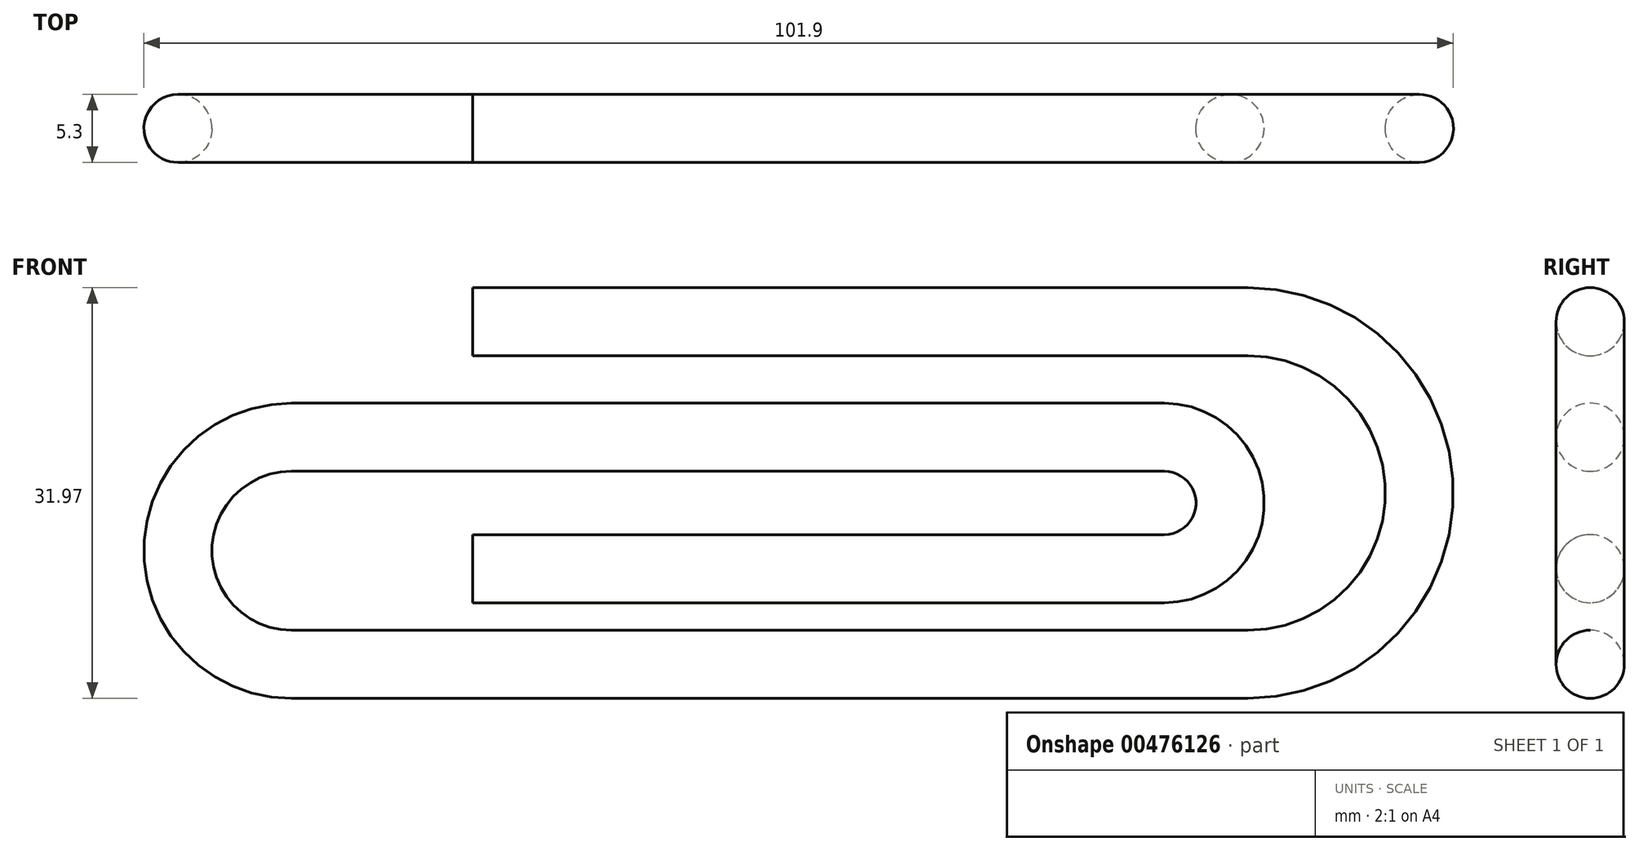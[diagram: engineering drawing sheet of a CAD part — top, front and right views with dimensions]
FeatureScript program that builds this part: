
annotation { "Feature Type Name" : "Feature", "Feature Type Description" : "" }
export const myFeature = defineFeature(function(context is Context, id is Id, definition is map)
    precondition{}
    {
        {
            var Q0;
            Q0=qCreatedBy(makeId("Front.planeOp"),FACE);
            cPlane(context, id + "F0", {"entities" : qUnion([Q0]), "cplaneType" : CPlaneType.OFFSET, "offset" : 25.4 * mm, "width" : 152.4 * mm, "height" : 152.4 * mm});
        }
        {
            var Q0;
            Q0=qCreatedBy(id+"F0.planeOp",FACE);
            var sketch = newSketch(context, id + "F1", { "sketchPlane" : qUnion([Q0])});
            skLineSegment(sketch, "E0", {"start": v(0, 0) * mm, "end": v(60.32, 0) * mm});
            skArc(sketch, "E1", {"start": v(60.32, -26.67) * mm, "mid": v(73.65, -13.34) * mm, "end": v(60.32, 0) * mm});
            skLineSegment(sketch, "E2", {"start": v(60.32, -26.67) * mm, "end": v(-14.11, -26.67) * mm});
            skArc(sketch, "E3", {"start": v(-14.11, -9) * mm, "mid": v(-22.95, -17.83) * mm, "end": v(-14.11, -26.67) * mm});
            skLineSegment(sketch, "E4", {"start": v(-14.11, -9) * mm, "end": v(53.8, -9) * mm});
            skArc(sketch, "E5", {"start": v(53.8, -19.23) * mm, "mid": v(58.92, -14.11) * mm, "end": v(53.8, -9) * mm});
            skLineSegment(sketch, "E6", {"start": v(53.8, -19.23) * mm, "end": v(0, -19.23) * mm});
            skSolve(sketch);
        }
        {
            var Q0;
            Q0=qCreatedBy(makeId("Right.planeOp"),FACE);
            var sketch = newSketch(context, id + "F2", { "sketchPlane" : qUnion([Q0])});
            skCircle(sketch, "E7", {"center": v(-25.1, 0) * mm, "radius": 2.65 * mm});
            skSolve(sketch);
        }
        {
            var Q0;
            Q0=makeQuery(id+"F2.imprint","IMPRINT",FACE,{"disambiguationData":[TD([[makeQuery(id+"F2.imprint","IMPRINT",EDGE,{"derivedFrom":sQuery(id+"F2.wireOp",EDGE,"E7")}),1.0]])]});
            var Q1;
            Q1=sQuery(id+"F1.wireOp",EDGE,"E0");
            var Q2;
            Q2=sQuery(id+"F1.wireOp",EDGE,"E1");
            var Q3;
            Q3=sQuery(id+"F1.wireOp",EDGE,"E2");
            var Q4;
            Q4=sQuery(id+"F1.wireOp",EDGE,"E3");
            var Q5;
            Q5=sQuery(id+"F1.wireOp",EDGE,"E4");
            var Q6;
            Q6=sQuery(id+"F1.wireOp",EDGE,"E5");
            var Q7;
            Q7=sQuery(id+"F1.wireOp",EDGE,"E6");
            sweep(context, id + "F3", {"profiles" : qUnion([Q0]), "path" : qUnion([Q1, Q2, Q3, Q4, Q5, Q6, Q7])});
        }
    });
